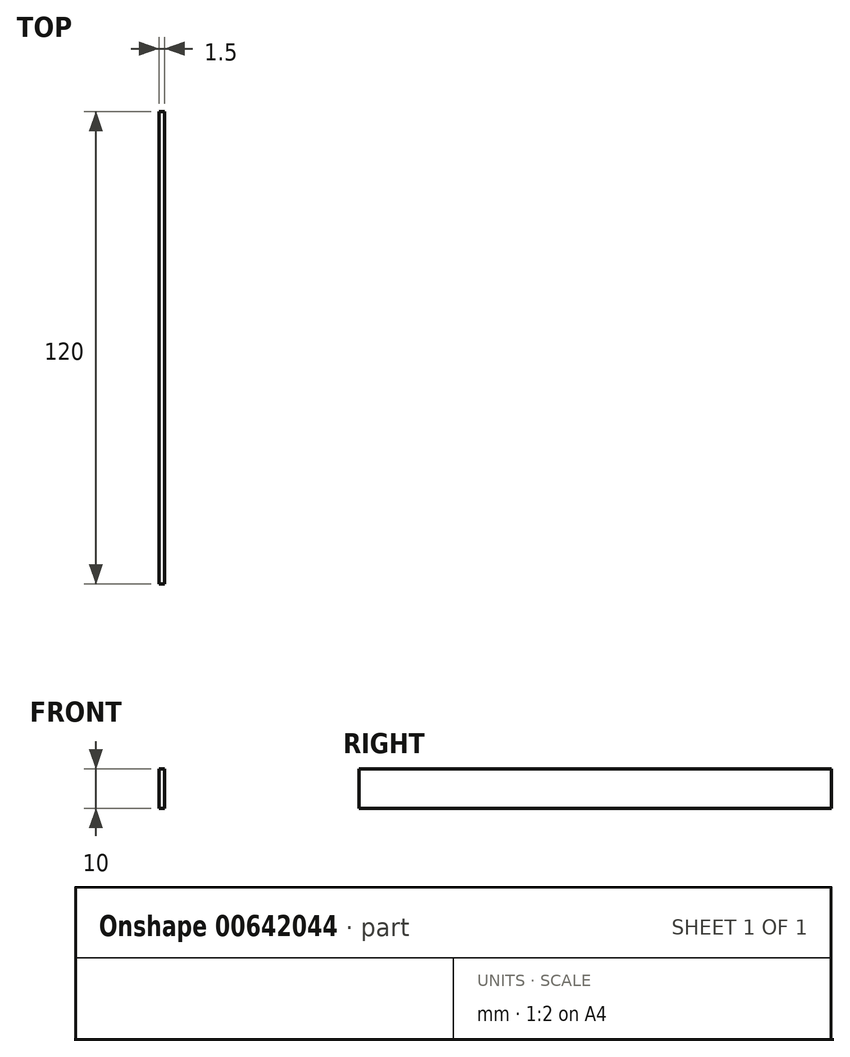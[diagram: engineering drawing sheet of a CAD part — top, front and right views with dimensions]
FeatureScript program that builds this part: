
annotation { "Feature Type Name" : "Feature", "Feature Type Description" : "" }
export const myFeature = defineFeature(function(context is Context, id is Id, definition is map)
    precondition{}
    {
        {
            var Q0;
            Q0=qCreatedBy(makeId("Right.planeOp"),FACE);
            var sketch = newSketch(context, id + "F0", { "sketchPlane" : qUnion([Q0])});
            skLineSegment(sketch, "E0.bottom", {"start": v(-62.08, -1.55) * mm, "end": v(57.92, -1.55) * mm});
            skLineSegment(sketch, "E0.top", {"start": v(-62.08, -11.55) * mm, "end": v(57.92, -11.55) * mm});
            skLineSegment(sketch, "E0.left", {"start": v(-62.08, -1.55) * mm, "end": v(-62.08, -11.55) * mm});
            skLineSegment(sketch, "E0.right", {"start": v(57.92, -1.55) * mm, "end": v(57.92, -11.55) * mm});
            skSolve(sketch);
        }
        {
            var Q0;
            Q0=makeQuery(id+"F0.imprint","IMPRINT",FACE,{"disambiguationData":[TD([[makeQuery(id+"F0.imprint","IMPRINT",EDGE,{"derivedFrom":sQuery(id+"F0.wireOp",EDGE,"E0.bottom")}),-1.0]])]});
            extrude(context, id + "F1", {"entities" : qUnion([Q0]), "depth" : 1.5 * mm, "offsetDistance" : 25 * mm});
        }
    });
